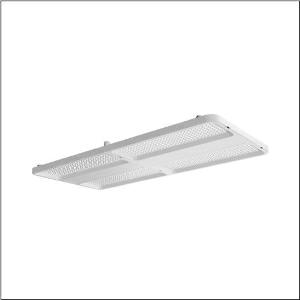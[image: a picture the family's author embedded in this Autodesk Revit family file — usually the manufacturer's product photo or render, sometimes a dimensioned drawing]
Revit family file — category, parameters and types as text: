
# Revit family: highbay_21_maxi_52hn12db4mba
name_source: partatom
category: Lighting Fixtures
units: mm (PartAtom-declared; Revit-internal decimal feet)

## family parameters
Cut with Voids When Loaded = No
Host = Face
Light Source = No
Part Type = Normal
Room Calculation Point = No
Round Connector Dimension = Use Diameter
Shared = No

## types (1)
- --- (1 x LED, 4230 lm, 22.6 W, 4000K)
    Apparent Load = 23 VA
    CIE Flux Codes = 90 98 100 100 100
    Color Rendering = 80
    Color Temperature = 4000K
    Default Elevation = 1800 mm
    Description = high bay luminaire Highbay 21 maxi; direct symmetric wide distribution, light control with lens of PMMA; UGR ≤ 22 (X = 4H | Y = 8H | S = 0.25H | reflection values 70/50/20); luminous flux: 28.000lm; light colour: 840, colour temperature: 4000K, MacAdam ≤ 3 SDCM (initial), colour rendering: CRI > 80; luminous efficacy: 194,4lm/W; rated service life: 75.000h (L80) at AT= ta max; control: DALI 2; luminaire connection: terminal, 5-pole, max. 2.5mm² (cable entry for one cable, Ø 8.5..16mm); mains connection: 230..240V, AC/DC 0/50..60Hz; connected load: 144W; protection rating (complete): IP40; insulation class (complete): insulation class I (protective earthing); protection symbol: D; impact resistance: IK08; certification: CE, ENEC, VDE, UKCA; luminaire for central battery installations according to EN 60598-2-22, internal wiring halogen-free; luminaire LABS conformity tested according to VDMA 24364:2018-05; ball impact resistant only with use of appropriate mounting accessories; Suitable for use in the food industry according to the specifications of IFS-Food, HACCP and/or BRC; housing frame of high-performance plastic PA6, matt traffic white (RAL 9016); cover of PMMA; dimension (LxWxH): 946 x 442 x 72mm; permissible operating ambient temperature: -40..+65°C (reducing of maximum allowable ambient temperature of 5°C with ceiling mounting); packaging unit: 1 piece; (delivery without accessories; please order mounting accessories separately)
    Height = 72 mm  [stored 0.23622 ft]
    Lamp = 1 x LED
    Lamp Light Flux = 4230 lm
    Lamp Power = 22.6 W
    Lamp count = 1
    Length = 946 mm
    Luminous efficacy = 187 lm/W
    Manufacturer = Siteco
    ModVariant = No
    Model = 52HN12DB4MBA
    Mounting Place = Ceiling
    Mounting Type = Pendant
    Number of Poles = 1
    OnlyDefault = Yes
    Power Factor = 1
    Product Name = Highbay 21 maxi
    Product group = high bay luminaire
    ProductGroupID = 902
    Protection Class = Protection class I
    Protection Degree = IP 40
    RLX_Detail_Level = 1
    RLX_Emergency_Light_Flux = 0 lm
    RLX_Emergency_Type = 0
    RLX_Emergency_Type_DB = No
    RlxData = <blob elided: 128321 chars, md5=11d8f8c2>
    Socket = socket
    Standby Power = 0 W
    System Light Flux = 4230 lm
    System Power = 23 W
    Type Comments = : DC mode (central or group accumulator) initial emergency light level
    Type Image = l_1376023.jpg
    URL = http://relux.com
    VarID = @adj_014509
    Voltage = 0 V
    Weight = 0.00 kg
    Width = 442 mm

note: [stored X ft] marks values corroborated as IEEE doubles in the binary element streams (Revit-internal decimal feet)

## geometry (parser evidence)
native form markers: Blend x4, Sweep x10
no freeform markers — native parametric forms only
